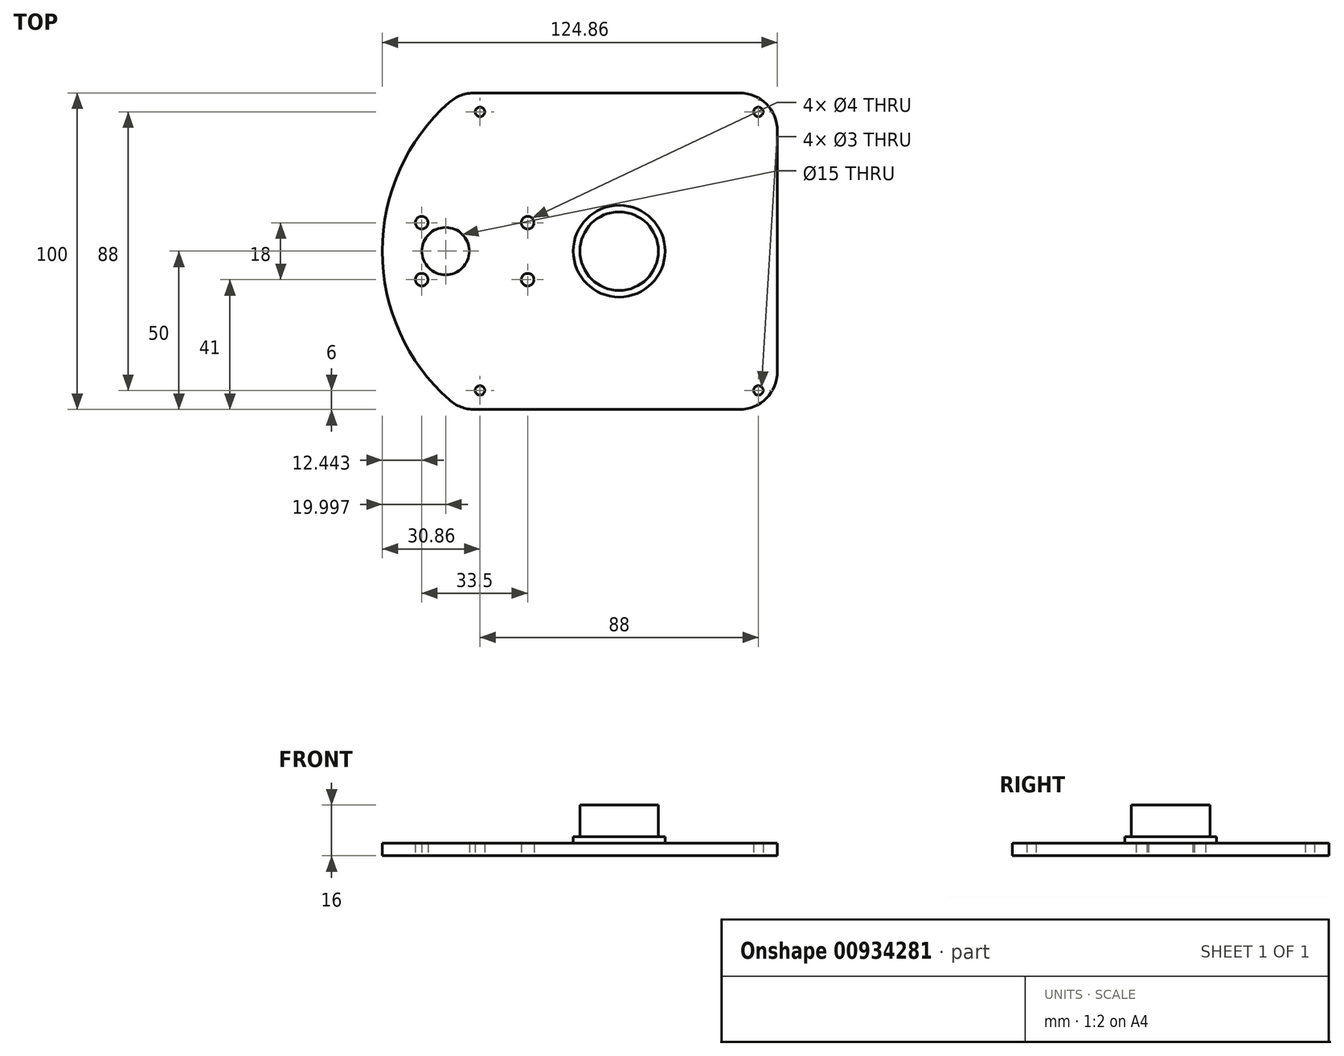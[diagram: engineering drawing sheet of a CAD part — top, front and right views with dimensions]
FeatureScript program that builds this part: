
annotation { "Feature Type Name" : "Feature", "Feature Type Description" : "" }
export const myFeature = defineFeature(function(context is Context, id is Id, definition is map)
    precondition{}
    {
        {
            var Q0;
            Q0=qCreatedBy(makeId("Top.planeOp"),FACE);
            var sketch = newSketch(context, id + "F0", { "sketchPlane" : qUnion([Q0])});
            skLineSegment(sketch, "E0.bottom", {"start": v(50, -50) * mm, "end": v(-50, -50) * mm});
            skLineSegment(sketch, "E0.top", {"start": v(50, 50) * mm, "end": v(-50, 50) * mm});
            skLineSegment(sketch, "E0.left", {"start": v(50, -50) * mm, "end": v(50, 50) * mm});
            skLineSegment(sketch, "E0.right", {"start": v(-50, -50) * mm, "end": v(-50, 50) * mm, "construction": true});
            skPoint(sketch, "E0.middle", {"position": v(0, 0) * mm});
            skLineSegment(sketch, "E1.bottom", {"start": v(47, -47) * mm, "end": v(-47, -47) * mm});
            skLineSegment(sketch, "E1.top", {"start": v(47, 47) * mm, "end": v(-47, 47) * mm});
            skLineSegment(sketch, "E1.left", {"start": v(47, -47) * mm, "end": v(47, 47) * mm});
            skLineSegment(sketch, "E1.right", {"start": v(-47, -47) * mm, "end": v(-47, 47) * mm});
            skLineSegment(sketch, "E2.bottom", {"start": v(-47, 47) * mm, "end": v(-44, 47) * mm, "construction": true});
            skLineSegment(sketch, "E2.top", {"start": v(-47, 44) * mm, "end": v(-44, 44) * mm, "construction": true});
            skLineSegment(sketch, "E2.left", {"start": v(-47, 47) * mm, "end": v(-47, 44) * mm, "construction": true});
            skLineSegment(sketch, "E2.right", {"start": v(-44, 47) * mm, "end": v(-44, 44) * mm, "construction": true});
            skLineSegment(sketch, "E3.bottom", {"start": v(47, 47) * mm, "end": v(44, 47) * mm, "construction": true});
            skLineSegment(sketch, "E3.top", {"start": v(47, 44) * mm, "end": v(44, 44) * mm, "construction": true});
            skLineSegment(sketch, "E3.left", {"start": v(47, 47) * mm, "end": v(47, 44) * mm, "construction": true});
            skLineSegment(sketch, "E3.right", {"start": v(44, 47) * mm, "end": v(44, 44) * mm, "construction": true});
            skLineSegment(sketch, "E4.bottom", {"start": v(47, -47) * mm, "end": v(44, -47) * mm, "construction": true});
            skLineSegment(sketch, "E4.top", {"start": v(47, -44) * mm, "end": v(44, -44) * mm, "construction": true});
            skLineSegment(sketch, "E4.left", {"start": v(47, -47) * mm, "end": v(47, -44) * mm, "construction": true});
            skLineSegment(sketch, "E4.right", {"start": v(44, -47) * mm, "end": v(44, -44) * mm, "construction": true});
            skLineSegment(sketch, "E5.bottom", {"start": v(-47, -47) * mm, "end": v(-44, -47) * mm, "construction": true});
            skLineSegment(sketch, "E5.top", {"start": v(-47, -44) * mm, "end": v(-44, -44) * mm, "construction": true});
            skLineSegment(sketch, "E5.left", {"start": v(-47, -47) * mm, "end": v(-47, -44) * mm, "construction": true});
            skLineSegment(sketch, "E5.right", {"start": v(-44, -47) * mm, "end": v(-44, -44) * mm, "construction": true});
            skCircle(sketch, "E6", {"center": v(-44, -44) * mm, "radius": 1.5 * mm});
            skCircle(sketch, "E7", {"center": v(-44, 44) * mm, "radius": 1.5 * mm});
            skCircle(sketch, "E8", {"center": v(44, 44) * mm, "radius": 1.5 * mm});
            skCircle(sketch, "E9", {"center": v(44, -44) * mm, "radius": 1.5 * mm});
            skCircle(sketch, "E10", {"center": v(-47, 47) * mm, "radius": 7.5 * mm});
            skCircle(sketch, "E11", {"center": v(47, 47) * mm, "radius": 7.5 * mm});
            skCircle(sketch, "E12", {"center": v(47, -47) * mm, "radius": 7.5 * mm});
            skCircle(sketch, "E13", {"center": v(-47, -47) * mm, "radius": 7.5 * mm});
            skCircle(sketch, "E14", {"center": v(0, 0) * mm, "radius": 14.5 * mm});
            skCircle(sketch, "E15", {"center": v(0, 0) * mm, "radius": 12.4 * mm});
            skArc(sketch, "E16", {"start": v(-50, 50) * mm, "mid": v(-74.86, 0) * mm, "end": v(-50, -50) * mm});
            skLineSegment(sketch, "E17", {"start": v(0, 0) * mm, "end": v(-99.84, 0) * mm, "construction": true});
            skLineSegment(sketch, "E18", {"start": v(-74.86, 0) * mm, "end": v(-54.86, 0) * mm});
            skCircle(sketch, "E19", {"center": v(-54.86, 0) * mm, "radius": 7.5 * mm});
            skLineSegment(sketch, "E20.bottom", {"start": v(-62.42, -9) * mm, "end": v(-47.3, -9) * mm});
            skLineSegment(sketch, "E20.top", {"start": v(-62.42, 9) * mm, "end": v(-47.3, 9) * mm, "construction": true});
            skLineSegment(sketch, "E20.left", {"start": v(-62.42, -9) * mm, "end": v(-62.42, 9) * mm, "construction": true});
            skLineSegment(sketch, "E20.right", {"start": v(-47.3, -9) * mm, "end": v(-47.3, 9) * mm});
            skLineSegment(sketch, "E21", {"start": v(-62.42, 9) * mm, "end": v(-54.86, 0) * mm, "construction": true});
            skLineSegment(sketch, "E22.bottom", {"start": v(-62.42, 9) * mm, "end": v(-28.92, 9) * mm, "construction": true});
            skLineSegment(sketch, "E22.top", {"start": v(-62.42, -9) * mm, "end": v(-28.92, -9) * mm, "construction": true});
            skLineSegment(sketch, "E22.left", {"start": v(-62.42, 9) * mm, "end": v(-62.42, -9) * mm, "construction": true});
            skLineSegment(sketch, "E22.right", {"start": v(-28.92, 9) * mm, "end": v(-28.92, -9) * mm, "construction": true});
            skCircle(sketch, "E23", {"center": v(-62.42, 9) * mm, "radius": 2 * mm});
            skCircle(sketch, "E24", {"center": v(-62.42, -9) * mm, "radius": 2 * mm});
            skCircle(sketch, "E25", {"center": v(-28.92, -9) * mm, "radius": 2 * mm});
            skCircle(sketch, "E26", {"center": v(-28.92, 9) * mm, "radius": 2 * mm});
            skSolve(sketch);
        }
        {
            var Q0;
            {var subQ0=sQuery(id+"F0.wireOp",EDGE,"E13");var subQ1=sQuery(id+"F0.wireOp",EDGE,"E0.right");var subQ2=makeQuery(id+"F0.imprint","INTERSECT",VERTEX,{"derivedFrom":[subQ1,subQ0]});Q0=makeQuery(id+"F0.imprint","IMPRINT",FACE,{"disambiguationData":[TD([[makeQuery(id+"F0.imprint","IMPRINT",EDGE,{"disambiguationData":[TD([[subQ2,-1.0]])],"derivedFrom":subQ1}),-1.0]])]});}
            var Q1;
            {var subQ5=sQuery(id+"F0.wireOp",EDGE,"E0.bottom");var subQ8=sQuery(id+"F0.wireOp",EDGE,"E0.right");var subQ9=makeQuery(id+"F0.imprint","INTERSECT",VERTEX,{"derivedFrom":[subQ5,subQ8]});Q1=makeQuery(id+"F0.imprint","IMPRINT",FACE,{"disambiguationData":[TD([[makeQuery(id+"F0.imprint","IMPRINT",EDGE,{"disambiguationData":[TD([[subQ9,1.0]])],"derivedFrom":subQ5}),-1.0]])]});}
            var Q2;
            Q2=makeQuery(id+"F0.imprint","IMPRINT",FACE,{"disambiguationData":[TD([[makeQuery(id+"F0.imprint","IMPRINT",EDGE,{"derivedFrom":sQuery(id+"F0.wireOp",EDGE,"E6")}),-1.0]])]});
            var Q3;
            {var subQ0=sQuery(id+"F0.wireOp",EDGE,"E12");var subQ1=sQuery(id+"F0.wireOp",EDGE,"E0.bottom");var subQ2=makeQuery(id+"F0.imprint","INTERSECT",VERTEX,{"derivedFrom":[subQ1,subQ0]});Q3=makeQuery(id+"F0.imprint","IMPRINT",FACE,{"disambiguationData":[TD([[makeQuery(id+"F0.imprint","IMPRINT",EDGE,{"disambiguationData":[TD([[subQ2,-1.0]])],"derivedFrom":subQ1}),-1.0]])]});}
            var Q4;
            {var subQ6=sQuery(id+"F0.wireOp",EDGE,"E0.left");var subQ7=sQuery(id+"F0.wireOp",EDGE,"E0.bottom");var subQ8=makeQuery(id+"F0.imprint","INTERSECT",VERTEX,{"derivedFrom":[subQ7,subQ6]});Q4=makeQuery(id+"F0.imprint","IMPRINT",FACE,{"disambiguationData":[TD([[makeQuery(id+"F0.imprint","IMPRINT",EDGE,{"disambiguationData":[TD([[subQ8,-1.0]])],"derivedFrom":subQ7}),-1.0]])]});}
            var Q5;
            Q5=makeQuery(id+"F0.imprint","IMPRINT",FACE,{"disambiguationData":[TD([[makeQuery(id+"F0.imprint","IMPRINT",EDGE,{"derivedFrom":sQuery(id+"F0.wireOp",EDGE,"E9")}),-1.0]])]});
            var Q6;
            {var subQ0=sQuery(id+"F0.wireOp",EDGE,"E12");var subQ1=sQuery(id+"F0.wireOp",EDGE,"E0.left");var subQ2=makeQuery(id+"F0.imprint","INTERSECT",VERTEX,{"derivedFrom":[subQ1,subQ0]});Q6=makeQuery(id+"F0.imprint","IMPRINT",FACE,{"disambiguationData":[TD([[makeQuery(id+"F0.imprint","IMPRINT",EDGE,{"disambiguationData":[TD([[subQ2,-1.0]])],"derivedFrom":subQ1}),1.0]])]});}
            var Q7;
            {var subQ6=sQuery(id+"F0.wireOp",EDGE,"E0.left");var subQ7=sQuery(id+"F0.wireOp",EDGE,"E0.top");var subQ8=makeQuery(id+"F0.imprint","INTERSECT",VERTEX,{"derivedFrom":[subQ7,subQ6]});Q7=makeQuery(id+"F0.imprint","IMPRINT",FACE,{"disambiguationData":[TD([[makeQuery(id+"F0.imprint","IMPRINT",EDGE,{"disambiguationData":[TD([[subQ8,-1.0]])],"derivedFrom":subQ7}),1.0]])]});}
            var Q8;
            Q8=makeQuery(id+"F0.imprint","IMPRINT",FACE,{"disambiguationData":[TD([[makeQuery(id+"F0.imprint","IMPRINT",EDGE,{"derivedFrom":sQuery(id+"F0.wireOp",EDGE,"E8")}),-1.0]])]});
            var Q9;
            {var subQ0=sQuery(id+"F0.wireOp",EDGE,"E11");var subQ1=sQuery(id+"F0.wireOp",EDGE,"E0.top");var subQ2=makeQuery(id+"F0.imprint","INTERSECT",VERTEX,{"derivedFrom":[subQ1,subQ0]});Q9=makeQuery(id+"F0.imprint","IMPRINT",FACE,{"disambiguationData":[TD([[makeQuery(id+"F0.imprint","IMPRINT",EDGE,{"disambiguationData":[TD([[subQ2,-1.0]])],"derivedFrom":subQ1}),1.0]])]});}
            var Q10;
            {var subQ6=sQuery(id+"F0.wireOp",EDGE,"E0.top");var subQ8=sQuery(id+"F0.wireOp",EDGE,"E0.right");var subQ9=makeQuery(id+"F0.imprint","INTERSECT",VERTEX,{"derivedFrom":[subQ6,subQ8]});Q10=makeQuery(id+"F0.imprint","IMPRINT",FACE,{"disambiguationData":[TD([[makeQuery(id+"F0.imprint","IMPRINT",EDGE,{"disambiguationData":[TD([[subQ9,1.0]])],"derivedFrom":subQ6}),1.0]])]});}
            var Q11;
            Q11=makeQuery(id+"F0.imprint","IMPRINT",FACE,{"disambiguationData":[TD([[makeQuery(id+"F0.imprint","IMPRINT",EDGE,{"derivedFrom":sQuery(id+"F0.wireOp",EDGE,"E7")}),-1.0]])]});
            var Q12;
            {var subQ10=sQuery(id+"F0.wireOp",EDGE,"E12");var subQ13=sQuery(id+"F0.wireOp",EDGE,"E1.bottom");var subQ14=makeQuery(id+"F0.imprint","INTERSECT",VERTEX,{"derivedFrom":[subQ13,subQ10]});Q12=makeQuery(id+"F0.imprint","IMPRINT",FACE,{"disambiguationData":[TD([[makeQuery(id+"F0.imprint","IMPRINT",EDGE,{"disambiguationData":[TD([[subQ14,-1.0]])],"derivedFrom":subQ13}),-1.0]])]});}
            var Q13;
            {var subQ0=sQuery(id+"F0.wireOp",EDGE,"E13");var subQ1=sQuery(id+"F0.wireOp",EDGE,"E0.right");var subQ2=makeQuery(id+"F0.imprint","INTERSECT",VERTEX,{"derivedFrom":[subQ1,subQ0]});Q13=makeQuery(id+"F0.imprint","IMPRINT",FACE,{"disambiguationData":[TD([[makeQuery(id+"F0.imprint","IMPRINT",EDGE,{"disambiguationData":[TD([[subQ2,-1.0]])],"derivedFrom":subQ1}),1.0]])]});}
            var Q14;
            {var subQ0=sQuery(id+"F0.wireOp",EDGE,"E16");var subQ3=sQuery(id+"F0.wireOp",EDGE,"E10");var subQ5=makeQuery(id+"F0.imprint","INTERSECT",VERTEX,{"derivedFrom":[subQ3,subQ0]});Q14=makeQuery(id+"F0.imprint","IMPRINT",FACE,{"disambiguationData":[TD([[makeQuery(id+"F0.imprint","IMPRINT",EDGE,{"disambiguationData":[TD([[subQ5,-1.0]])],"derivedFrom":subQ3}),1.0]])]});}
            var Q15;
            {var subQ0=sQuery(id+"F0.wireOp",EDGE,"E16");var subQ3=sQuery(id+"F0.wireOp",EDGE,"E13");var subQ5=makeQuery(id+"F0.imprint","INTERSECT",VERTEX,{"derivedFrom":[subQ3,subQ0]});Q15=makeQuery(id+"F0.imprint","IMPRINT",FACE,{"disambiguationData":[TD([[makeQuery(id+"F0.imprint","IMPRINT",EDGE,{"disambiguationData":[TD([[subQ5,1.0]])],"derivedFrom":subQ3}),1.0]])]});}
            var Q16;
            {var subQ7=sQuery(id+"F0.wireOp",EDGE,"E0.right");var subQ9=sQuery(id+"F0.wireOp",EDGE,"E20.top");var subQ10=makeQuery(id+"F0.imprint","INTERSECT",VERTEX,{"derivedFrom":[subQ7,subQ9]});Q16=makeQuery(id+"F0.imprint","IMPRINT",FACE,{"disambiguationData":[TD([[makeQuery(id+"F0.imprint","IMPRINT",EDGE,{"disambiguationData":[TD([[subQ10,-1.0]])],"derivedFrom":subQ7}),1.0]])]});}
            var Q17;
            {var subQ0=sQuery(id+"F0.wireOp",EDGE,"E19");var subQ5=sQuery(id+"F0.wireOp",EDGE,"E0.right");var subQ6=makeQuery(id+"F0.imprint","INTERSECT",VERTEX,{"disambiguationData":[OD(1.0)],"derivedFrom":[subQ5,subQ0]});Q17=makeQuery(id+"F0.imprint","IMPRINT",FACE,{"disambiguationData":[TD([[makeQuery(id+"F0.imprint","IMPRINT",EDGE,{"disambiguationData":[TD([[subQ6,-1.0]])],"derivedFrom":subQ5}),1.0]])]});}
            var Q18;
            {var subQ0=sQuery(id+"F0.wireOp",EDGE,"E19");var subQ1=sQuery(id+"F0.wireOp",EDGE,"E0.right");var subQ2=makeQuery(id+"F0.imprint","INTERSECT",VERTEX,{"disambiguationData":[OD(0.0)],"derivedFrom":[subQ1,subQ0]});Q18=makeQuery(id+"F0.imprint","IMPRINT",FACE,{"disambiguationData":[TD([[makeQuery(id+"F0.imprint","IMPRINT",EDGE,{"disambiguationData":[TD([[subQ2,-1.0]])],"derivedFrom":subQ1}),1.0]])]});}
            var Q19;
            {var subQ3=sQuery(id+"F0.wireOp",EDGE,"E0.right");var subQ7=sQuery(id+"F0.wireOp",EDGE,"E20.bottom");var subQ9=makeQuery(id+"F0.imprint","INTERSECT",VERTEX,{"derivedFrom":[subQ3,subQ7]});Q19=makeQuery(id+"F0.imprint","IMPRINT",FACE,{"disambiguationData":[TD([[makeQuery(id+"F0.imprint","IMPRINT",EDGE,{"disambiguationData":[TD([[subQ9,-1.0]])],"derivedFrom":subQ3}),1.0]])]});}
            var Q20;
            {var subQ0=sQuery(id+"F0.wireOp",EDGE,"E19");var subQ1=sQuery(id+"F0.wireOp",EDGE,"E0.right");var subQ2=makeQuery(id+"F0.imprint","INTERSECT",VERTEX,{"disambiguationData":[OD(0.0)],"derivedFrom":[subQ1,subQ0]});Q20=makeQuery(id+"F0.imprint","IMPRINT",FACE,{"disambiguationData":[TD([[makeQuery(id+"F0.imprint","IMPRINT",EDGE,{"disambiguationData":[TD([[subQ2,-1.0]])],"derivedFrom":subQ1}),-1.0]])]});}
            var Q21;
            {var subQ0=sQuery(id+"F0.wireOp",EDGE,"E20.right");Q21=makeQuery(id+"F0.imprint","IMPRINT",FACE,{"disambiguationData":[TD([[makeQuery(id+"F0.imprint","IMPRINT",EDGE,{"derivedFrom":subQ0}),1.0]])]});}
            var Q22;
            Q22=makeQuery(id+"F0.imprint","IMPRINT",FACE,{"disambiguationData":[TD([[makeQuery(id+"F0.imprint","IMPRINT",EDGE,{"derivedFrom":sQuery(id+"F0.wireOp",EDGE,"E19")}),-1.0]])]});
            extrude(context, id + "F1", {"entities" : qUnion([Q0, Q1, Q2, Q3, Q4, Q5, Q6, Q7, Q8, Q9, Q10, Q11, Q12, Q13, Q14, Q15, Q16, Q17, Q18, Q19, Q20, Q21, Q22]), "depth" : 4 * mm, "offsetDistance" : 25 * mm});
        }
        {
            var Q0;
            Q0=makeQuery(id+"F1.opExtrude","SWEPT_EDGE",EDGE,{"disambiguationData":[OSD([sQuery(id+"F0.wireOp",EDGE,"E0.top"),sQuery(id+"F0.wireOp",EDGE,"E0.right")])]});
            var Q1;
            Q1=makeQuery(id+"F1.opExtrude","SWEPT_EDGE",EDGE,{"disambiguationData":[OSD([sQuery(id+"F0.wireOp",EDGE,"E0.top"),sQuery(id+"F0.wireOp",EDGE,"E0.left")])]});
            var Q2;
            Q2=makeQuery(id+"F1.opExtrude","SWEPT_EDGE",EDGE,{"disambiguationData":[OSD([sQuery(id+"F0.wireOp",EDGE,"E0.bottom"),sQuery(id+"F0.wireOp",EDGE,"E0.left")])]});
            var Q3;
            Q3=makeQuery(id+"F1.opExtrude","SWEPT_EDGE",EDGE,{"disambiguationData":[OSD([sQuery(id+"F0.wireOp",EDGE,"E0.bottom"),sQuery(id+"F0.wireOp",EDGE,"E0.right")])]});
            fillet(context, id + "F2", {"entities" : qUnion([Q0, Q1, Q2, Q3]), "radius" : 12 * mm, "tangentPropagation" : true, "allowEdgeOverflow" : false});
        }
        {
            var Q0;
            Q0=makeQuery(id+"F0.imprint","IMPRINT",FACE,{"disambiguationData":[TD([[makeQuery(id+"F0.imprint","IMPRINT",EDGE,{"derivedFrom":sQuery(id+"F0.wireOp",EDGE,"E14")}),1.0]])]});
            extrude(context, id + "F3", {"entities" : qUnion([Q0]), "operationType" : NewBodyOperationType.ADD, "depth" : 6 * mm, "offsetDistance" : 25 * mm});
        }
        {
            var Q0;
            Q0=makeQuery(id+"F0.imprint","IMPRINT",FACE,{"disambiguationData":[TD([[makeQuery(id+"F0.imprint","IMPRINT",EDGE,{"derivedFrom":sQuery(id+"F0.wireOp",EDGE,"E15")}),1.0]])]});
            extrude(context, id + "F4", {"entities" : qUnion([Q0]), "operationType" : NewBodyOperationType.ADD, "depth" : 16 * mm, "offsetDistance" : 25 * mm});
        }
    });
